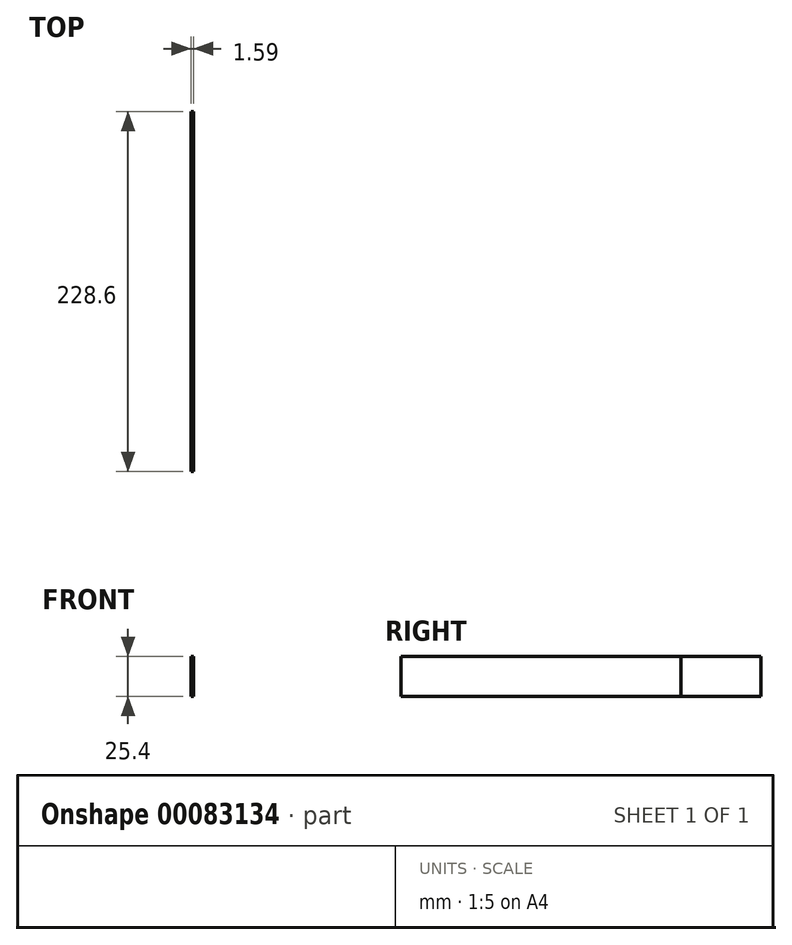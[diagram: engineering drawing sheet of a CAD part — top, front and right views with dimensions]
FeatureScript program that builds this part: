
annotation { "Feature Type Name" : "Feature", "Feature Type Description" : "" }
export const myFeature = defineFeature(function(context is Context, id is Id, definition is map)
    precondition{}
    {
        {
            var Q0;
            Q0=qCreatedBy(makeId("Front.planeOp"),FACE);
            var sketch = newSketch(context, id + "F0", { "sketchPlane" : qUnion([Q0])});
            skLineSegment(sketch, "E0.bottom", {"start": v(0, 0) * mm, "end": v(1.59, 0) * mm});
            skLineSegment(sketch, "E0.top", {"start": v(0, 25.4) * mm, "end": v(1.59, 25.4) * mm});
            skLineSegment(sketch, "E0.left", {"start": v(0, 0) * mm, "end": v(0, 25.4) * mm});
            skLineSegment(sketch, "E0.right", {"start": v(1.59, 0) * mm, "end": v(1.59, 25.4) * mm});
            skSolve(sketch);
        }
        {
            var Q0;
            Q0=qSketchRegion(id+"F0",true);
            extrude(context, id + "F1", {"entities" : qUnion([Q0]), "depth" : 228.6 * mm});
        }
        {
            var Q0;
            Q0=qSketchRegion(id+"F0",true);
            extrude(context, id + "F2", {"entities" : qUnion([Q0]), "depth" : 50.8 * mm});
        }
        {
            var Q0;
            Q0 = qSketchRegion(id + "F0", true);
            extrude(context, id + "F3", {"entities" : qUnion([Q0]), "depth" : 25.4 * mm});
        }
        {
            var Q0;
            Q0=makeQuery(id+"F3.opExtrude","SWEPT_BODY",BODY,{"disambiguationData":[OSD([sQuery(id+"F0.wireOp",EDGE,"E0.bottom"),sQuery(id+"F0.wireOp",EDGE,"E0.top"),sQuery(id+"F0.wireOp",EDGE,"E0.left"),sQuery(id+"F0.wireOp",EDGE,"E0.right")])]});
            deleteBodies(context, id + "F4", {"entities" : qUnion([Q0])});
        }
    });
